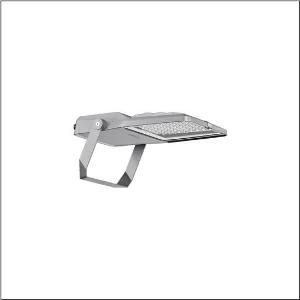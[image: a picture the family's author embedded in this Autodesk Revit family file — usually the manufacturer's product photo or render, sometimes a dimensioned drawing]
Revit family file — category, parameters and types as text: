
# Revit family: floodlight_fl_21_iq_mini___pl52_5xa7772d4d1a_6062
name_source: partatom
category: Lighting Fixtures
units: mm (PartAtom-declared; Revit-internal decimal feet)

## family parameters
Cut with Voids When Loaded = No
Host = Face
Light Source = No
Part Type = Normal
Room Calculation Point = No
Round Connector Dimension = Use Diameter
Shared = No

## types (1)
- --- (1 x LED, 18610 lm, 143 W, 4000K)
    Apparent Load = 143 VA
    CIE Flux Codes = 26 60 98 100 100
    Color Rendering = 70
    Color Temperature = 4000K
    Default Elevation = 1800 mm
    Description = Floodlight FL 21 iQ mini, floodlight, primary light control with lens, of PMMA, primary optical cover: protective disc, of toughened safety glass, transparent, light distribution: PL52, light emission: direct distribution, installation type: surface-mounted, lamps: LED, High Power LED, rated values: 18.610lm | 143W | 130,1lm/W (begin service life); end service life: 18.610lm | 151,6W; at 50% lumin. flux: 9.305lm | 60,8W | 153lm/W, colour temperature: 4000K, colour rendering: CRI > 70, light colour: 740, light setting 1 begin service life: 100% | 18.610lm | 143W | 130,1lm/W | 4.000K, light setting 1 end service life: 151,6W, further light settings possible, control: Street-Remote, Auto-Match, Temp-Guard, Night-Set, Smart-Wire, Desk-Remote (wireless, voltage-free reading and setting of iQ features in the workshop via application-optimized NFC function/RFID function), optimised constant luminous flux control (CLO 2.0), pre-setting: linear dimming characteristic, with terminal, 6-pole, mains connection: 220..240V, AC, 50/60Hz, luminaire housing, of diecast aluminium, powder-coated, SITECO metallic grey (DB 702S), corrosivity category C5 mid according to DIN EN ISO 12944suitable for swimming poolschlorine-resistant, sealing non-destructively replaceable, mounting bracket, of steel, galvanised, powder-coated, SITECO metallic grey (DB 702S), protection rating (complete): IP66, insulation class (complete): insulation class II (safety insulation), certification: CE, ENEC, VDE, protection symbol: D, impact resistance: IK08, permissible operating ambient temperature: -40..+40°C, permissible operating ambient temperature for outdoor applications: -40..+50°C, standard: DIN EN 12944, LABS conformity tested according to VDMA 24364:2018-05, packaging unit: 1 piece

Light Distribution: PL52
    Height = 70 mm
    Lamp = 1 x LED
    Lamp Light Flux = 18610 lm
    Lamp Power = 143 W
    Lamp count = 1
    Length = 485 mm
    Luminous efficacy = 130 lm/W
    Manufacturer = Siteco
    ModVariant = No
    Model = 5XA7772D4D1A
    Mounting Place = Pole
    Mounting Type = Pole annexe
    Number of Poles = 1
    OnlyDefault = Yes
    Power Factor = 1
    Product Name = Floodlight FL 21 iQ mini | PL52
    Product group = floodlight | pylon annexe
    ProductGroupID = 6201
    Protection Class = Protection class II
    Protection Degree = IP 66
    RLX_Detail_Level = 1
    RLX_Emergency_Light_Flux = 0 lm
    RLX_Emergency_Type = 0
    RLX_Emergency_Type_DB = No
    RlxData = <blob elided: 97021 chars, md5=0a41dc4b>
    Socket = socket
    Standby Power = 0 W
    System Light Flux = 18610 lm
    System Power = 143 W
    Type Comments = factory setting: luminous flux: 100 % | dim-lin: 254 | 730 mA
    Type Image = l_1006845.jpg
    URL = http://relux.com
    VarID = @adj_164661
    Voltage = 0 V
    Weight = 0.00 kg
    Width = 337 mm

## geometry (parser evidence)
native form markers: Blend x4, Sweep x12
no freeform markers — native parametric forms only
